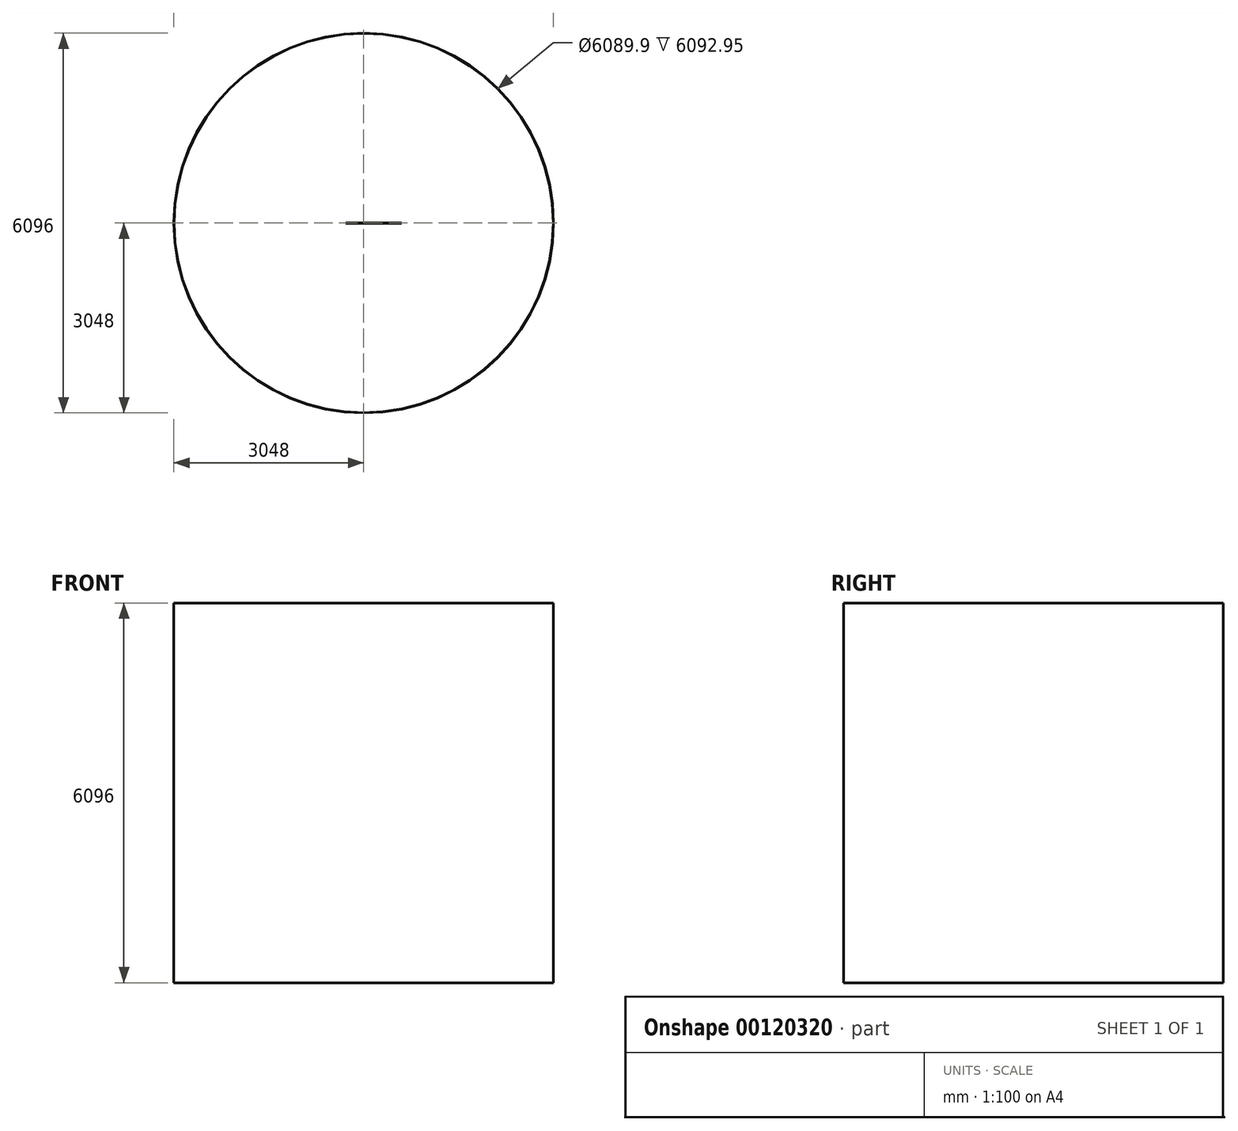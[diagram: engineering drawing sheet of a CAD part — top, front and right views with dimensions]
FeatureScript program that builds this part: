
annotation { "Feature Type Name" : "Feature", "Feature Type Description" : "" }
export const myFeature = defineFeature(function(context is Context, id is Id, definition is map)
    precondition{}
    {
        {
            var Q0;
            Q0=qCreatedBy(makeId("Top.planeOp"),FACE);
            var sketch = newSketch(context, id + "F0", { "sketchPlane" : qUnion([Q0])});
            skCircle(sketch, "E0", {"center": v(0, 0) * mm, "radius": 3048 * mm});
            skSolve(sketch);
        }
        {
            var Q0;
            Q0=makeQuery(id+"F0.imprint","IMPRINT",FACE,{"disambiguationData":[TD([[makeQuery(id+"F0.imprint","IMPRINT",EDGE,{"derivedFrom":sQuery(id+"F0.wireOp",EDGE,"E0")}),1.0]])]});
            extrude(context, id + "F1", {"entities" : qUnion([Q0]), "depth" : 6096 * mm});
        }
        {
            var Q0;
            Q0=makeQuery(id+"F1.opExtrude","CAP_FACE",FACE,{"disambiguationData":[OSD([sQuery(id+"F0.wireOp",EDGE,"E0")])],"isStart":false});
            shell(context, id + "F2", {"entities" : qUnion([Q0]), "thickness" : 3.05 * mm});
        }
        {
            var Q0;
            Q0=qCreatedBy(makeId("Right.planeOp"),FACE);
            var sketch = newSketch(context, id + "F3", { "sketchPlane" : qUnion([Q0])});
            skCircle(sketch, "E1", {"center": v(0, 0) * mm, "radius": 114.3 * mm});
            skSolve(sketch);
        }
        {
            var Q0;
            Q0=sQuery(id+"F3.wireOp",EDGE,"E1");
            extrude(context, id + "F4", {"bodyType" : ToolBodyType.SURFACE, "surfaceEntities" : qUnion([Q0]), "depth" : 914.4 * mm});
        }
        {
            var Q0;
            Q0=makeQuery(id+"F4.opExtrude","SWEPT_BODY",BODY,{"disambiguationData":[OSD([sQuery(id+"F3.wireOp",EDGE,"E1")])]});
            transform(context, id + "F5", {"entities" : qUnion([Q0]), "transformType" : TransformType.TRANSLATION_3D, "dx" : -291.86 * mm, "dy" : 0 * mm, "dz" : 261.14 * mm, "makeCopy" : false});
        }
        {
            var Q0;
            Q0=qCreatedBy(makeId("Top.planeOp"),FACE);
            var sketch = newSketch(context, id + "F6", { "sketchPlane" : qUnion([Q0])});
            skLineSegment(sketch, "E2.bottom", {"start": v(-286.51, 0) * mm, "end": v(610.18, 0) * mm});
            skLineSegment(sketch, "E2.top", {"start": v(-286.51, -4.76) * mm, "end": v(610.18, -4.76) * mm});
            skLineSegment(sketch, "E2.left", {"start": v(-286.51, 0) * mm, "end": v(-286.51, -4.76) * mm});
            skLineSegment(sketch, "E2.right", {"start": v(610.18, 0) * mm, "end": v(610.18, -4.76) * mm});
            skSolve(sketch);
        }
        {
            var Q0;
            Q0 = qSketchRegion(id + "F6", true);
            extrude(context, id + "F7", {"entities" : qUnion([Q0]), "operationType" : NewBodyOperationType.REMOVE, "depth" : 1734.82 * mm});
        }
    });
